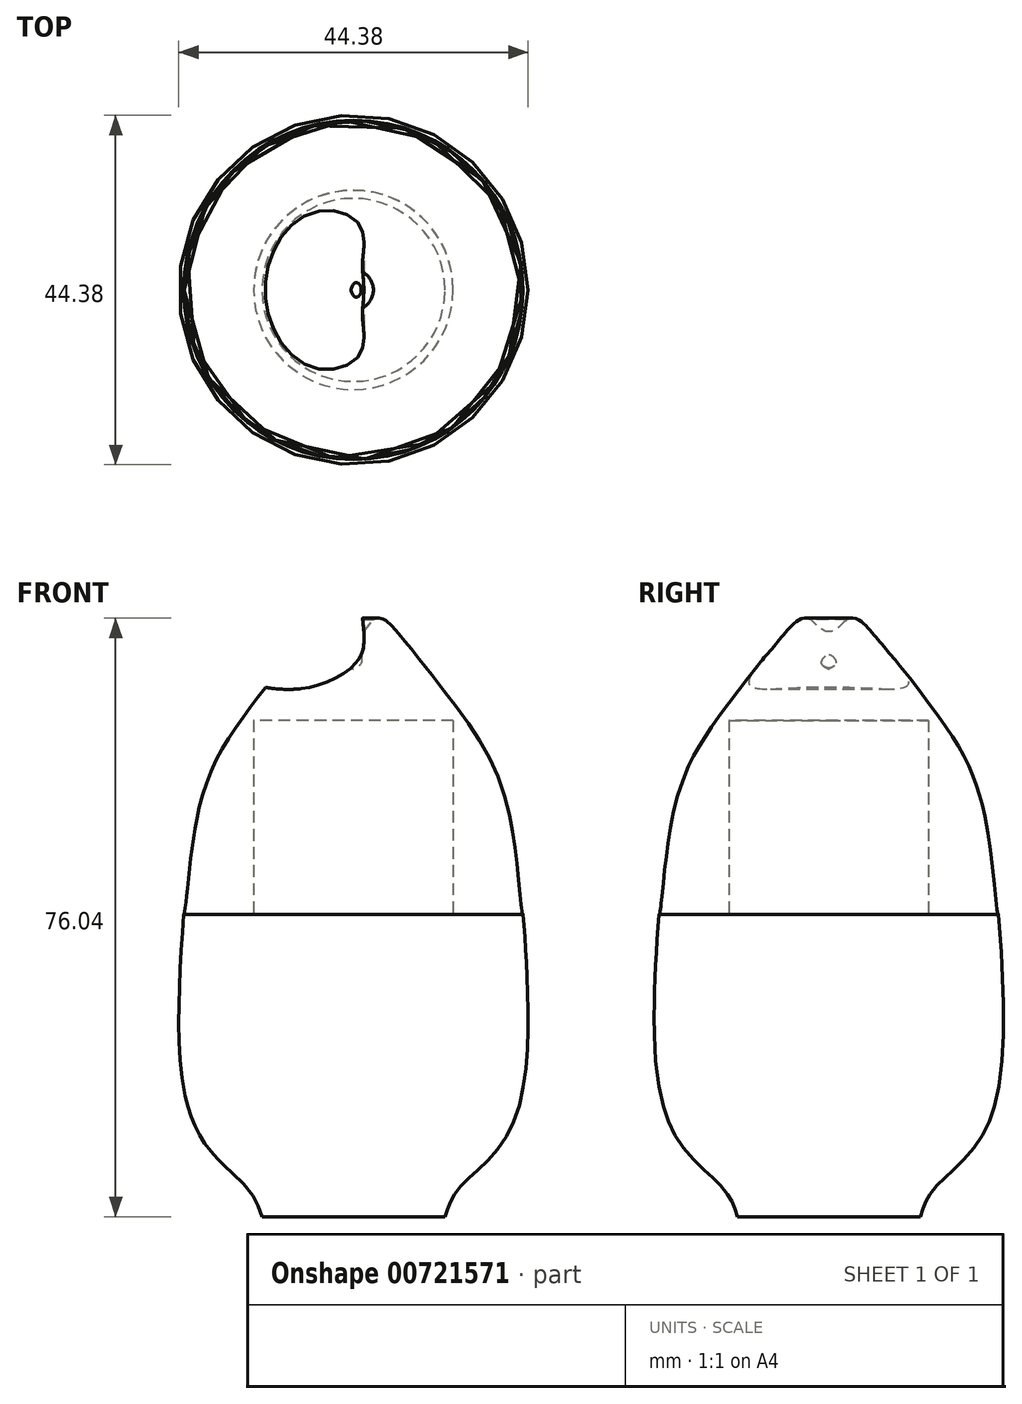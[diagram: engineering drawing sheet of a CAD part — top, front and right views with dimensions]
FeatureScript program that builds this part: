
annotation { "Feature Type Name" : "Feature", "Feature Type Description" : "" }
export const myFeature = defineFeature(function(context is Context, id is Id, definition is map)
    precondition{}
    {
        {
            var Q0;
            Q0=qCreatedBy(makeId("Front.planeOp"),FACE);
            var sketch = newSketch(context, id + "F0", { "sketchPlane" : qUnion([Q0])});
            skFitSpline(sketch, "E0", {"points": [v(-21.55, 0) * mm, v(-22.1, -9.2) * mm, v(-19.9, -27.4) * mm, v(-13.28, -34.98) * mm, v(-11.63, -38.42) * mm], "startDerivative": vector(-2.53, -32.8) * mm, "endDerivative": vector(6.55, -21.65) * mm});
            skLineSegment(sketch, "E1", {"start": v(-11.63, -38.42) * mm, "end": v(0, -38.42) * mm});
            skLineSegment(sketch, "E2", {"start": v(0, -38.42) * mm, "end": v(0, 0) * mm});
            skLineSegment(sketch, "E3", {"start": v(0, 0) * mm, "end": v(-21.55, 0) * mm});
            skLineSegment(sketch, "E4", {"start": v(0, 39.76) * mm, "end": v(0, -42.18) * mm, "construction": true});
            skSolve(sketch);
        }
        {
            var Q0;
            Q0=makeQuery(id+"F0.imprint","IMPRINT",FACE,{"disambiguationData":[TD([[makeQuery(id+"F0.imprint","IMPRINT",EDGE,{"derivedFrom":sQuery(id+"F0.wireOp",EDGE,"E0")}),1.0]])]});
            var Q1;
            Q1=sQuery(id+"F0.wireOp",EDGE,"E4");
            revolve(context, id + "F1", {"surfaceOperationType" : NewSurfaceOperationType.NEW, "entities" : qUnion([Q0]), "axis" : qUnion([Q1]), "revolveType" : RevolveType.FULL});
        }
        {
            var Q0;
            Q0=qCreatedBy(makeId("Front.planeOp"),FACE);
            var sketch = newSketch(context, id + "F2", { "sketchPlane" : qUnion([Q0])});
            skFitSpline(sketch, "E5", {"points": [v(2.54, 37.45) * mm, v(3.62, 37.57) * mm, v(6.76, 34.44) * mm, v(14.35, 24.56) * mm, v(19.77, 12.75) * mm, v(21.5, 0) * mm, v(21.53, 0) * mm], "startDerivative": vector(13.85, 4.95) * mm, "endDerivative": vector(2.4, 1.34) * mm});
            skLineSegment(sketch, "E6", {"start": v(2.54, 37.45) * mm, "end": v(0.95, 35.4) * mm});
            skFitSpline(sketch, "E7", {"points": [v(0.95, 35.4) * mm, v(0.95, 33.37) * mm, v(0.95, 31.85) * mm, v(0, 31.15) * mm], "startDerivative": vector(-0.25, -5.37) * mm, "endDerivative": vector(-4.09, -1.94) * mm});
            skLineSegment(sketch, "E8", {"start": v(0, 31.15) * mm, "end": v(0, 0) * mm});
            skLineSegment(sketch, "E9", {"start": v(0, 0) * mm, "end": v(21.52, 0) * mm});
            skSolve(sketch);
        }
        {
            var Q0;
            Q0 = qSketchRegion(id + "F2", true);
            var Q1;
            Q1=sQuery(id+"F0.wireOp",EDGE,"E4");
            revolve(context, id + "F3", {"surfaceOperationType" : NewSurfaceOperationType.NEW, "entities" : qUnion([Q0]), "axis" : qUnion([Q1]), "revolveType" : RevolveType.FULL, "oppositeDirection" : true});
        }
        {
            var Q0;
            Q0=qCreatedBy(makeId("Front.planeOp"),FACE);
            var sketch = newSketch(context, id + "F4", { "sketchPlane" : qUnion([Q0])});
            skFitSpline(sketch, "E10", {"points": [v(1.14, 37.68) * mm, v(1.3, 34.14) * mm, v(0, 31.56) * mm, v(-4.43, 29.12) * mm, v(-7.97, 28.57) * mm, v(-11.16, 28.82) * mm, v(-14.1, 29.53) * mm, v(-14.1, 29.63) * mm], "startDerivative": vector(2.82, -22.76) * mm, "endDerivative": vector(1.68, 3.54) * mm});
            skLineSegment(sketch, "E11", {"start": v(-14.1, 29.53) * mm, "end": v(-1.59, 41.18) * mm});
            skLineSegment(sketch, "E12", {"start": v(-1.59, 41.18) * mm, "end": v(1.14, 37.68) * mm});
            skSolve(sketch);
        }
        {
            var Q0;
            Q0 = qSketchRegion(id + "F4", true);
            extrude(context, id + "F5", {"entities" : qUnion([Q0]), "operationType" : NewBodyOperationType.REMOVE, "oppositeDirection" : true, "depth" : 25.4 * mm, "offsetDistance" : 25.4 * mm});
        }
        {
            var Q0;
            Q0 = qSketchRegion(id + "F4", true);
            extrude(context, id + "F6", {"entities" : qUnion([Q0]), "operationType" : NewBodyOperationType.REMOVE, "depth" : 18.62 * mm, "offsetDistance" : 25.4 * mm});
        }
        {
            var Q0;
            Q0=qCreatedBy(makeId("Top.planeOp"),FACE);
            var sketch = newSketch(context, id + "F7", { "sketchPlane" : qUnion([Q0])});
            skCircle(sketch, "E13", {"center": v(0, 0) * mm, "radius": 12.67 * mm});
            skSolve(sketch);
        }
        {
            var Q0;
            Q0 = qSketchRegion(id + "F7", true);
            extrude(context, id + "F8", {"entities" : qUnion([Q0]), "operationType" : NewBodyOperationType.REMOVE, "depth" : 24.64 * mm, "offsetDistance" : 25.4 * mm});
        }
    });
